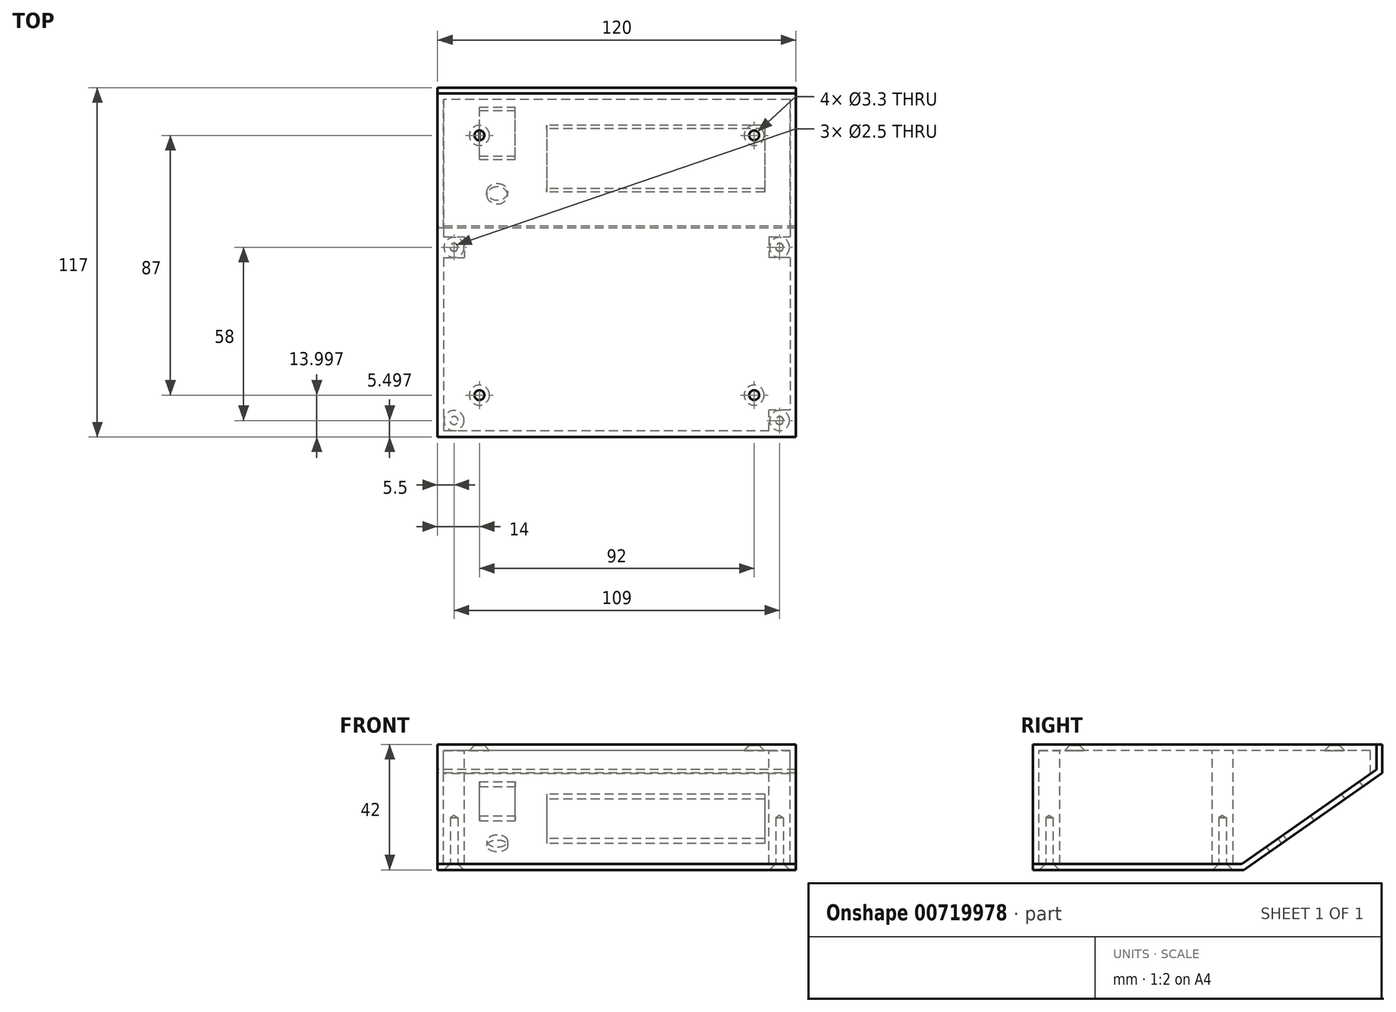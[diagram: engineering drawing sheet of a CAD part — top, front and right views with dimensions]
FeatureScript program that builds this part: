
annotation { "Feature Type Name" : "Feature", "Feature Type Description" : "" }
export const myFeature = defineFeature(function(context is Context, id is Id, definition is map)
    precondition{}
    {
        {
            var Q0;
            Q0=qCreatedBy(makeId("Right.planeOp"),FACE);
            var sketch = newSketch(context, id + "F0", { "sketchPlane" : qUnion([Q0])});
            skLineSegment(sketch, "E0.bottom", {"start": v(34.97, 0) * mm, "end": v(-34.97, 0) * mm});
            skLineSegment(sketch, "E0.top", {"start": v(34.97, 40) * mm, "end": v(-34.97, 40) * mm});
            skLineSegment(sketch, "E0.left", {"start": v(34.97, 0) * mm, "end": v(34.97, 40) * mm});
            skLineSegment(sketch, "E0.right", {"start": v(-34.97, 0) * mm, "end": v(-34.97, 40) * mm});
            skLineSegment(sketch, "E1", {"start": v(34.97, 0) * mm, "end": v(80.03, 31.55) * mm});
            skLineSegment(sketch, "E2", {"start": v(80.03, 31.55) * mm, "end": v(80.03, 40) * mm});
            skLineSegment(sketch, "E3", {"start": v(80.03, 40) * mm, "end": v(34.97, 40) * mm});
            skLineSegment(sketch, "E4.0", {"start": v(35.6, -2) * mm, "end": v(-34.97, -2) * mm});
            skLineSegment(sketch, "E4.1", {"start": v(35.6, -2) * mm, "end": v(82.03, 30.5) * mm});
            skLineSegment(sketch, "E4.2", {"start": v(82.03, 30.5) * mm, "end": v(82.03, 40) * mm});
            skLineSegment(sketch, "E5", {"start": v(-34.97, -2) * mm, "end": v(-34.97, 0) * mm});
            skLineSegment(sketch, "E6", {"start": v(80.03, 40) * mm, "end": v(82.03, 40) * mm});
            skSolve(sketch);
        }
        {
            var Q0;
            Q0=makeQuery(id+"F0.imprint","IMPRINT",FACE,{"disambiguationData":[TD([[makeQuery(id+"F0.imprint","IMPRINT",EDGE,{"derivedFrom":sQuery(id+"F0.wireOp",EDGE,"E0.bottom")}),-1.0]])]});
            var Q1;
            Q1=makeQuery(id+"F0.imprint","IMPRINT",FACE,{"disambiguationData":[TD([[makeQuery(id+"F0.imprint","IMPRINT",EDGE,{"derivedFrom":sQuery(id+"F0.wireOp",EDGE,"E0.left")}),-1.0]])]});
            extrude(context, id + "F1", {"entities" : qUnion([Q0, Q1]), "depth" : 120 * mm, "offsetDistance" : 25 * mm});
        }
        {
            var Q0;
            Q0=makeQuery(id+"F1.opExtrude","SWEPT_FACE",FACE,{"disambiguationData":[OSD([sQuery(id+"F0.wireOp",EDGE,"E0.bottom")])]});
            var Q1;
            Q1=makeQuery(id+"F1.opExtrude","SWEPT_FACE",FACE,{"disambiguationData":[OSD([sQuery(id+"F0.wireOp",EDGE,"E1")])]});
            shell(context, id + "F2", {"entities" : qUnion([Q0, Q1]), "thickness" : 2 * mm});
        }
        {
            var Q0;
            Q0=makeQuery(id+"F2.opShell","OFFSET_FACE",FACE,{"disambiguationData":[OSD([sQuery(id+"F0.wireOp",EDGE,"E0.top"),sQuery(id+"F0.wireOp",EDGE,"E3")])]});
            var sketch = newSketch(context, id + "F3", { "sketchPlane" : qUnion([Q0])});
            skLineSegment(sketch, "E7.bottom", {"start": v(2, 32.97) * mm, "end": v(118, 32.97) * mm});
            skLineSegment(sketch, "E7.top", {"start": v(2, -32.03) * mm, "end": v(118, -32.03) * mm});
            skLineSegment(sketch, "E7.left", {"start": v(2, 32.97) * mm, "end": v(2, -32.03) * mm});
            skLineSegment(sketch, "E7.right", {"start": v(118, 32.97) * mm, "end": v(118, -32.03) * mm});
            skLineSegment(sketch, "E8.bottom", {"start": v(2, 32.97) * mm, "end": v(9, 32.97) * mm});
            skLineSegment(sketch, "E8.top", {"start": v(2, 25.97) * mm, "end": v(9, 25.97) * mm});
            skLineSegment(sketch, "E8.left", {"start": v(2, 32.97) * mm, "end": v(2, 25.97) * mm});
            skLineSegment(sketch, "E8.right", {"start": v(9, 32.97) * mm, "end": v(9, 25.97) * mm});
            skLineSegment(sketch, "E9", {"start": v(2, 0.47) * mm, "end": v(118, 0.47) * mm, "construction": true});
            skLineSegment(sketch, "E10", {"start": v(60, -32.03) * mm, "end": v(60, 32.97) * mm, "construction": true});
            skLineSegment(sketch, "E11.MirrorCS", {"start": v(118, 25.97) * mm, "end": v(111, 25.97) * mm});
            skLineSegment(sketch, "E12.MirrorCS", {"start": v(118, 32.97) * mm, "end": v(118, 25.97) * mm});
            skLineSegment(sketch, "E13.MirrorCS", {"start": v(118, 32.97) * mm, "end": v(111, 32.97) * mm});
            skLineSegment(sketch, "E14.MirrorCS", {"start": v(111, 32.97) * mm, "end": v(111, 25.97) * mm});
            skLineSegment(sketch, "E15.MirrorCS", {"start": v(2, -25.03) * mm, "end": v(9, -25.03) * mm});
            skLineSegment(sketch, "E16.MirrorCS", {"start": v(2, -32.03) * mm, "end": v(2, -25.03) * mm});
            skLineSegment(sketch, "E17.MirrorCS", {"start": v(2, -32.03) * mm, "end": v(9, -32.03) * mm});
            skLineSegment(sketch, "E18.MirrorCS", {"start": v(9, -32.03) * mm, "end": v(9, -25.03) * mm});
            skLineSegment(sketch, "E19.MirrorCS", {"start": v(111, -32.03) * mm, "end": v(111, -25.03) * mm});
            skLineSegment(sketch, "E20.MirrorCS", {"start": v(118, -32.03) * mm, "end": v(111, -32.03) * mm});
            skLineSegment(sketch, "E21.MirrorCS", {"start": v(118, -32.03) * mm, "end": v(118, -25.03) * mm});
            skLineSegment(sketch, "E22.MirrorCS", {"start": v(118, -25.03) * mm, "end": v(111, -25.03) * mm});
            skLineSegment(sketch, "E23", {"start": v(118, -32.03) * mm, "end": v(111, -25.03) * mm, "construction": true});
            skLineSegment(sketch, "E24", {"start": v(111, -32.03) * mm, "end": v(118, -25.03) * mm, "construction": true});
            skLineSegment(sketch, "E25.MirrorCS", {"start": v(2, -32.03) * mm, "end": v(9, -25.03) * mm, "construction": true});
            skLineSegment(sketch, "E26.MirrorCS", {"start": v(9, -32.03) * mm, "end": v(2, -25.03) * mm, "construction": true});
            skLineSegment(sketch, "E27.MirrorCS", {"start": v(118, 32.97) * mm, "end": v(111, 25.97) * mm, "construction": true});
            skLineSegment(sketch, "E28.MirrorCS", {"start": v(111, 32.97) * mm, "end": v(118, 25.97) * mm, "construction": true});
            skLineSegment(sketch, "E29.MirrorCS", {"start": v(9, 32.97) * mm, "end": v(2, 25.97) * mm, "construction": true});
            skLineSegment(sketch, "E30.MirrorCS", {"start": v(2, 32.97) * mm, "end": v(9, 25.97) * mm, "construction": true});
            skLineSegment(sketch, "E31", {"start": v(106, 32.97) * mm, "end": v(106, -78.03) * mm, "construction": true});
            skLineSegment(sketch, "E32", {"start": v(2, -66.03) * mm, "end": v(118, -66.03) * mm, "construction": true});
            skLineSegment(sketch, "E33", {"start": v(2, 20.97) * mm, "end": v(118, 20.97) * mm, "construction": true});
            skLineSegment(sketch, "E34", {"start": v(14, 32.97) * mm, "end": v(14, -78.03) * mm, "construction": true});
            skPoint(sketch, "E35", {"position": v(106, 20.97) * mm});
            skPoint(sketch, "E36", {"position": v(106, -66.03) * mm});
            skPoint(sketch, "E37", {"position": v(14, -66.03) * mm});
            skPoint(sketch, "E38", {"position": v(14, 20.97) * mm});
            skSolve(sketch);
        }
        {
            var Q0;
            Q0=makeQuery(id+"F3.imprint","IMPRINT",FACE,{"disambiguationData":[TD([[makeQuery(id+"F3.imprint","IMPRINT",EDGE,{"derivedFrom":sQuery(id+"F3.wireOp",EDGE,"E8.bottom")}),1.0]])]});
            var Q1;
            Q1=makeQuery(id+"F3.imprint","IMPRINT",FACE,{"disambiguationData":[TD([[makeQuery(id+"F3.imprint","IMPRINT",EDGE,{"derivedFrom":sQuery(id+"F3.wireOp",EDGE,"E11.MirrorCS")}),-1.0]])]});
            var Q2;
            Q2=makeQuery(id+"F3.imprint","IMPRINT",FACE,{"disambiguationData":[TD([[makeQuery(id+"F3.imprint","IMPRINT",EDGE,{"derivedFrom":sQuery(id+"F3.wireOp",EDGE,"E15.MirrorCS")}),-1.0]])]});
            var Q3;
            Q3=makeQuery(id+"F3.imprint","IMPRINT",FACE,{"disambiguationData":[TD([[makeQuery(id+"F3.imprint","IMPRINT",EDGE,{"derivedFrom":sQuery(id+"F3.wireOp",EDGE,"E19.MirrorCS")}),-1.0]])]});
            var Q4;
            Q4=makeQuery(id+"F1.opExtrude","SWEPT_FACE",FACE,{"disambiguationData":[OSD([sQuery(id+"F0.wireOp",EDGE,"E0.bottom")])]});
            extrude(context, id + "F4", {"entities" : qUnion([Q0, Q1, Q2, Q3]), "operationType" : NewBodyOperationType.ADD, "endBound" : BoundingType.UP_TO_SURFACE, "depth" : 25 * mm, "endBoundEntityFace" : qUnion([Q4]), "offsetDistance" : 25 * mm});
        }
        {
            var Q0;
            Q0=makeQuery(id+"F0.imprint","IMPRINT",FACE,{"disambiguationData":[TD([[makeQuery(id+"F0.imprint","IMPRINT",EDGE,{"derivedFrom":sQuery(id+"F0.wireOp",EDGE,"E0.bottom")}),1.0]])]});
            var Q1;
            Q1=sQuery(id+"F0.wireOp",EDGE,"E5");
            var Q2;
            Q2=makeQuery(id+"F1.opExtrude","CAP_FACE",FACE,{"disambiguationData":[OSD([sQuery(id+"F0.wireOp",EDGE,"E0.bottom"),sQuery(id+"F0.wireOp",EDGE,"E0.top"),sQuery(id+"F0.wireOp",EDGE,"E0.right"),sQuery(id+"F0.wireOp",EDGE,"E1"),sQuery(id+"F0.wireOp",EDGE,"E2"),sQuery(id+"F0.wireOp",EDGE,"E3")])],"isStart":false});
            extrude(context, id + "F5", {"entities" : qUnion([Q0]), "surfaceEntities" : qUnion([Q1]), "endBound" : BoundingType.UP_TO_SURFACE, "depth" : 25 * mm, "endBoundEntityFace" : qUnion([Q2]), "offsetDistance" : 25 * mm});
        }
        {
            var Q0;
            Q0=makeQuery(id+"F5.opExtrude","SWEPT_FACE",FACE,{"disambiguationData":[OSD([sQuery(id+"F0.wireOp",EDGE,"E4.1")])]});
            var sketch = newSketch(context, id + "F6", { "sketchPlane" : qUnion([Q0])});
            skCircle(sketch, "E39", {"center": v(20, -42.02) * mm, "radius": 3.5 * mm});
            skLineSegment(sketch, "E40", {"start": v(20, -28.02) * mm, "end": v(20, -84.69) * mm, "construction": true});
            skLineSegment(sketch, "E41.bottom", {"start": v(113, -74.35) * mm, "end": v(33, -74.35) * mm, "construction": true});
            skLineSegment(sketch, "E41.top", {"start": v(113, -38.35) * mm, "end": v(33, -38.35) * mm, "construction": true});
            skLineSegment(sketch, "E41.left", {"start": v(113, -74.35) * mm, "end": v(113, -38.35) * mm, "construction": true});
            skLineSegment(sketch, "E41.right", {"start": v(33, -74.35) * mm, "end": v(33, -38.35) * mm, "construction": true});
            skLineSegment(sketch, "E42.bottom", {"start": v(120, -84.69) * mm, "end": v(0, -84.69) * mm, "construction": true});
            skLineSegment(sketch, "E42.top", {"start": v(120, -28.02) * mm, "end": v(0, -28.02) * mm, "construction": true});
            skLineSegment(sketch, "E42.left", {"start": v(120, -84.69) * mm, "end": v(120, -28.02) * mm, "construction": true});
            skLineSegment(sketch, "E42.right", {"start": v(0, -84.69) * mm, "end": v(0, -28.02) * mm, "construction": true});
            skLineSegment(sketch, "E43", {"start": v(120, -56.35) * mm, "end": v(0, -56.35) * mm, "construction": true});
            skLineSegment(sketch, "E44.bottom", {"start": v(109.5, -69.35) * mm, "end": v(36.5, -69.35) * mm});
            skLineSegment(sketch, "E44.top", {"start": v(109.5, -43.35) * mm, "end": v(36.5, -43.35) * mm});
            skLineSegment(sketch, "E44.left", {"start": v(109.5, -69.35) * mm, "end": v(109.5, -43.35) * mm});
            skLineSegment(sketch, "E44.right", {"start": v(36.5, -69.35) * mm, "end": v(36.5, -43.35) * mm});
            skLineSegment(sketch, "E45.bottom", {"start": v(14, -56.69) * mm, "end": v(26, -56.69) * mm});
            skLineSegment(sketch, "E45.top", {"start": v(14, -76.69) * mm, "end": v(26, -76.69) * mm});
            skLineSegment(sketch, "E45.left", {"start": v(14, -56.69) * mm, "end": v(14, -76.69) * mm});
            skLineSegment(sketch, "E45.right", {"start": v(26, -56.69) * mm, "end": v(26, -76.69) * mm});
            skSolve(sketch);
        }
        {
            var Q0;
            Q0=makeQuery(id+"F6.imprint","IMPRINT",FACE,{"disambiguationData":[TD([[makeQuery(id+"F6.imprint","IMPRINT",EDGE,{"derivedFrom":sQuery(id+"F6.wireOp",EDGE,"E44.bottom")}),-1.0]])]});
            var Q1;
            Q1=makeQuery(id+"F6.imprint","IMPRINT",FACE,{"disambiguationData":[TD([[makeQuery(id+"F6.imprint","IMPRINT",EDGE,{"derivedFrom":sQuery(id+"F6.wireOp",EDGE,"E39")}),1.0]])]});
            var Q2;
            Q2=makeQuery(id+"F6.imprint","IMPRINT",FACE,{"disambiguationData":[TD([[makeQuery(id+"F6.imprint","IMPRINT",EDGE,{"derivedFrom":sQuery(id+"F6.wireOp",EDGE,"E45.bottom")}),-1.0]])]});
            extrude(context, id + "F7", {"entities" : qUnion([Q0, Q1, Q2]), "operationType" : NewBodyOperationType.REMOVE, "endBound" : BoundingType.UP_TO_NEXT, "oppositeDirection" : true, "depth" : 25 * mm, "offsetDistance" : 25 * mm});
        }
        {
            var Q0;
            Q0=makeQuery(id+"F5.opExtrude","SWEPT_FACE",FACE,{"disambiguationData":[OSD([sQuery(id+"F0.wireOp",EDGE,"E4.0")])]});
            var sketch = newSketch(context, id + "F8", { "sketchPlane" : qUnion([Q0])});
            skPoint(sketch, "E46.0", {"position": v(114.5, -28.53) * mm});
            skPoint(sketch, "E47.0", {"position": v(114.5, 29.47) * mm});
            skPoint(sketch, "E48.0", {"position": v(5.5, -28.53) * mm});
            skPoint(sketch, "E49.0", {"position": v(5.5, 29.47) * mm});
            skSolve(sketch);
        }
        {
            var Q0;
            Q0=sQuery(id+"F8.wireOp",VERTEX,"E46.0");
            var Q1;
            Q1=sQuery(id+"F8.wireOp",VERTEX,"E47.0");
            var Q2;
            Q2=sQuery(id+"F8.wireOp",VERTEX,"E49.0");
            var Q3;
            Q3=sQuery(id+"F8.wireOp",VERTEX,"E48.0");
            var Q4;
            Q4=makeQuery(id+"F1.opExtrude","SWEPT_BODY",BODY,{"disambiguationData":[OSD([sQuery(id+"F0.wireOp",EDGE,"E0.bottom"),sQuery(id+"F0.wireOp",EDGE,"E0.top"),sQuery(id+"F0.wireOp",EDGE,"E0.right"),sQuery(id+"F0.wireOp",EDGE,"E1"),sQuery(id+"F0.wireOp",EDGE,"E2"),sQuery(id+"F0.wireOp",EDGE,"E3")])]});
            var Q5;
            Q5=makeQuery(id+"F5.opExtrude","SWEPT_BODY",BODY,{"disambiguationData":[OSD([sQuery(id+"F0.wireOp",EDGE,"E0.bottom"),sQuery(id+"F0.wireOp",EDGE,"E1"),sQuery(id+"F0.wireOp",EDGE,"E2"),sQuery(id+"F0.wireOp",EDGE,"E4.0"),sQuery(id+"F0.wireOp",EDGE,"E4.1"),sQuery(id+"F0.wireOp",EDGE,"E4.2"),sQuery(id+"F0.wireOp",EDGE,"E5"),sQuery(id+"F0.wireOp",EDGE,"E6")])]});
            hole(context, id + "F9", {"style" : HoleStyle.C_SINK, "endStyle" : HoleEndStyle.BLIND, "standardTappedOrClearance" : lookupTablePath({ "standard" : "ISO", "engagement" : "75%", "pitch" : "0.5 mm", "size" : "M3", "type" : "Tapped" }), "standardBlindInLast" : lookupTablePath({ "standard" : "ISO", "engagement" : "75%", "pitch" : "0.5 mm", "size" : "M3", "type" : "Tapped" }), "holeDiameter" : 2.5 * mm, "cSinkDiameter" : 6.72 * mm, "cSinkAngle" : 90 * degree, "majorDiameter" : 3 * mm, "showTappedDepth" : true, "holeDepth" : 17.5 * mm, "isTappedThrough" : true, "tappedDepth" : 16 * mm, "tapClearance" : 3, "startFromSketch" : true, "locations" : qUnion([Q0, Q1, Q2, Q3]), "scope" : qUnion([Q4, Q5])});
        }
        {
            var Q0;
            Q0=sQuery(id+"F3.wireOp",VERTEX,"E38");
            var Q1;
            Q1=sQuery(id+"F3.wireOp",VERTEX,"E35");
            var Q2;
            Q2=sQuery(id+"F3.wireOp",VERTEX,"E36");
            var Q3;
            Q3=sQuery(id+"F3.wireOp",VERTEX,"E37");
            var Q4;
            Q4=makeQuery(id+"F1.opExtrude","SWEPT_BODY",BODY,{"disambiguationData":[OSD([sQuery(id+"F0.wireOp",EDGE,"E0.bottom"),sQuery(id+"F0.wireOp",EDGE,"E0.top"),sQuery(id+"F0.wireOp",EDGE,"E0.right"),sQuery(id+"F0.wireOp",EDGE,"E1"),sQuery(id+"F0.wireOp",EDGE,"E2"),sQuery(id+"F0.wireOp",EDGE,"E3")])]});
            hole(context, id + "F10", {"style" : HoleStyle.C_SINK, "endStyle" : HoleEndStyle.BLIND, "standardTappedOrClearance" : lookupTablePath({ "standard" : "ISO", "fit" : "Normal", "size" : "M3", "type" : "Clearance" }), "standardBlindInLast" : lookupTablePath({ "fit" : "Standard", "standard" : "ISO", "size" : "M3", "type" : "Clearance" }), "holeDiameter" : 3.3 * mm, "cSinkDiameter" : 6.72 * mm, "cSinkAngle" : 90 * degree, "majorDiameter" : 5 * mm, "holeDepth" : 25 * mm, "isTappedThrough" : true, "tappedDepth" : 12 * mm, "tapClearance" : 3, "startFromSketch" : true, "locations" : qUnion([Q0, Q1, Q2, Q3]), "scope" : qUnion([Q4])});
        }
    });
